# Revit family: Gohome_CoveLounge_R21
name_source: partatom
category: Furniture
units: mm (PartAtom-declared; Revit-internal decimal feet)

## family parameters
Always vertical = Yes
Cut with Voids When Loaded = No
OmniClass Number = 23.40.20.00
OmniClass Title = General Furniture and Specialties
Room Calculation Point = No
Shared = No
Work Plane-Based = No

## types (2) — shared parameters
Back Material = <By Category>
Cushion Material = <By Category>
Depth = 660 mm  [stored 2.16535 ft]
Height = 725 mm  [stored 2.37861 ft]
Manufacturer = gohome
Model = Cove Lounge
Seat Material = <By Category>
URL = www.gohome.com.au
zero-valued in all types: Default Elevation

## per-type parameters (varying)
| type | 3 Seater | Width |
| 2.5 Seater | No | 1800 mm  [stored 5.90551 ft] |
| 3 Seater | Yes | 2200 mm |

type visibility flags (boolean, named after types; folded from table):
- 2.5 Seater: Yes: 2.5 Seater
- 3 Seater: Yes: (none)

note: [stored X ft] marks values corroborated as IEEE doubles in the binary element streams (Revit-internal decimal feet)

## geometry (parser evidence)
native form markers: Sweep x2
no freeform markers — native parametric forms only
